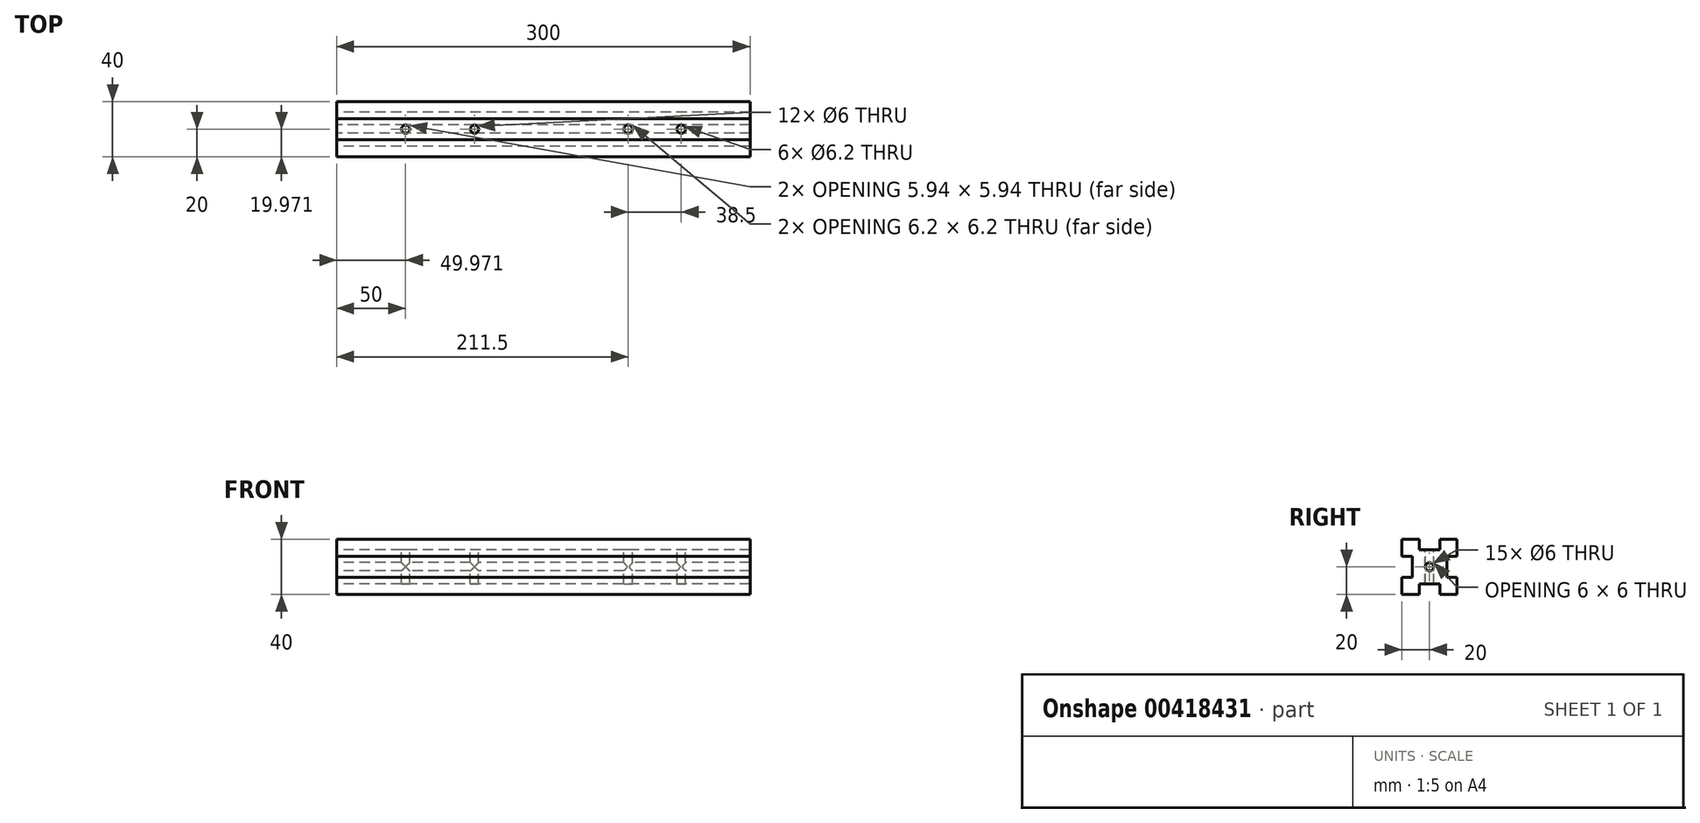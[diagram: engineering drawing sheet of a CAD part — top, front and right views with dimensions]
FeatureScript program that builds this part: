
annotation { "Feature Type Name" : "Feature", "Feature Type Description" : "" }
export const myFeature = defineFeature(function(context is Context, id is Id, definition is map)
    precondition{}
    {
        {
            var Q0;
            Q0=qCreatedBy(makeId("Right.planeOp"),FACE);
            var sketch = newSketch(context, id + "F0", { "sketchPlane" : qUnion([Q0])});
            skLineSegment(sketch, "E0.bottom", {"start": v(20, 20) * mm, "end": v(7.5, 20) * mm});
            skLineSegment(sketch, "E0.top", {"start": v(20, -20) * mm, "end": v(7.5, -20) * mm});
            skLineSegment(sketch, "E0.left", {"start": v(20, 20) * mm, "end": v(20, 7.5) * mm});
            skLineSegment(sketch, "E0.right", {"start": v(-20, 20) * mm, "end": v(-20, 7.5) * mm});
            skPoint(sketch, "E0.middle", {"position": v(0, 0) * mm});
            skLineSegment(sketch, "E1.top", {"start": v(7.5, 12.5) * mm, "end": v(-7.5, 12.5) * mm});
            skLineSegment(sketch, "E1.left", {"start": v(7.5, 20) * mm, "end": v(7.5, 12.5) * mm});
            skLineSegment(sketch, "E1.right", {"start": v(-7.5, 20) * mm, "end": v(-7.5, 12.5) * mm});
            skPoint(sketch, "E1.middle", {"position": v(0, 20) * mm});
            skLineSegment(sketch, "E2.bottom", {"start": v(20, 7.5) * mm, "end": v(12.5, 7.5) * mm});
            skLineSegment(sketch, "E2.top", {"start": v(20, -7.5) * mm, "end": v(12.5, -7.5) * mm});
            skLineSegment(sketch, "E2.right", {"start": v(12.5, 7.5) * mm, "end": v(12.5, -7.5) * mm});
            skPoint(sketch, "E2.middle", {"position": v(20, 0) * mm});
            skLineSegment(sketch, "E3.bottom", {"start": v(7.5, -12.5) * mm, "end": v(-7.5, -12.5) * mm});
            skLineSegment(sketch, "E3.left", {"start": v(7.5, -12.5) * mm, "end": v(7.5, -20) * mm});
            skLineSegment(sketch, "E3.right", {"start": v(-7.5, -12.5) * mm, "end": v(-7.5, -20) * mm});
            skPoint(sketch, "E3.middle", {"position": v(0, -20) * mm});
            skLineSegment(sketch, "E4.bottom", {"start": v(-12.5, 7.5) * mm, "end": v(-20, 7.5) * mm});
            skLineSegment(sketch, "E4.top", {"start": v(-12.5, -7.5) * mm, "end": v(-20, -7.5) * mm});
            skLineSegment(sketch, "E4.left", {"start": v(-12.5, 7.5) * mm, "end": v(-12.5, -7.5) * mm});
            skPoint(sketch, "E4.middle", {"position": v(-20, 0) * mm});
            skLineSegment(sketch, "E5.trimOffspring", {"start": v(-7.5, 20) * mm, "end": v(-20, 20) * mm});
            skPoint(sketch, "E6.orphan", {"position": v(7.5, 27.5) * mm});
            skPoint(sketch, "E7.orphan", {"position": v(-7.5, 27.5) * mm});
            skPoint(sketch, "E4.right.start.orphan", {"position": v(-27.5, 7.5) * mm});
            skLineSegment(sketch, "E8.trimOffspring", {"start": v(-20, -7.5) * mm, "end": v(-20, -20) * mm});
            skPoint(sketch, "E9.orphan", {"position": v(-27.5, -7.5) * mm});
            skLineSegment(sketch, "E10.trimOffspring", {"start": v(-7.5, -20) * mm, "end": v(-20, -20) * mm});
            skPoint(sketch, "E3.top.end.orphan", {"position": v(-7.5, -27.5) * mm});
            skPoint(sketch, "E11.orphan", {"position": v(7.5, -27.5) * mm});
            skLineSegment(sketch, "E12.trimOffspring", {"start": v(20, -7.5) * mm, "end": v(20, -20) * mm});
            skPoint(sketch, "E2.left.end.orphan", {"position": v(27.5, -7.5) * mm});
            skPoint(sketch, "E13.orphan", {"position": v(27.5, 7.5) * mm});
            skCircle(sketch, "E14", {"center": v(0, 0) * mm, "radius": 3 * mm});
            skSolve(sketch);
        }
        {
            var Q0;
            Q0 = qSketchRegion(id + "F0", true);
            extrude(context, id + "F1", {"entities" : qUnion([Q0]), "depth" : 300 * mm});
        }
        {
            var Q0;
            Q0=makeQuery(id+"F1.opExtrude","SWEPT_FACE",FACE,{"disambiguationData":[OSD([sQuery(id+"F0.wireOp",EDGE,"E1.top")])]});
            var sketch = newSketch(context, id + "F2", { "sketchPlane" : qUnion([Q0])});
            skCircle(sketch, "E15", {"center": v(250, 0) * mm, "radius": 3.1 * mm});
            skCircle(sketch, "E16", {"center": v(211.5, 0) * mm, "radius": 3.1 * mm});
            skSolve(sketch);
        }
        {
            var Q0;
            Q0 = qSketchRegion(id + "F2", true);
            extrude(context, id + "F3", {"entities" : qUnion([Q0]), "operationType" : NewBodyOperationType.REMOVE, "oppositeDirection" : true, "depth" : 50 * mm});
        }
        {
            var Q0;
            Q0=makeQuery(id+"F1.opExtrude","SWEPT_FACE",FACE,{"disambiguationData":[OSD([sQuery(id+"F0.wireOp",EDGE,"E1.top")])]});
            var sketch = newSketch(context, id + "F4", { "sketchPlane" : qUnion([Q0])});
            skCircle(sketch, "E17", {"center": v(50, 0) * mm, "radius": 3 * mm});
            skCircle(sketch, "E18", {"center": v(100, 0) * mm, "radius": 3 * mm});
            skSolve(sketch);
        }
        {
            var Q0;
            Q0 = qSketchRegion(id + "F4", true);
            extrude(context, id + "F5", {"entities" : qUnion([Q0]), "operationType" : NewBodyOperationType.REMOVE, "oppositeDirection" : true, "depth" : 50 * mm});
        }
    });
